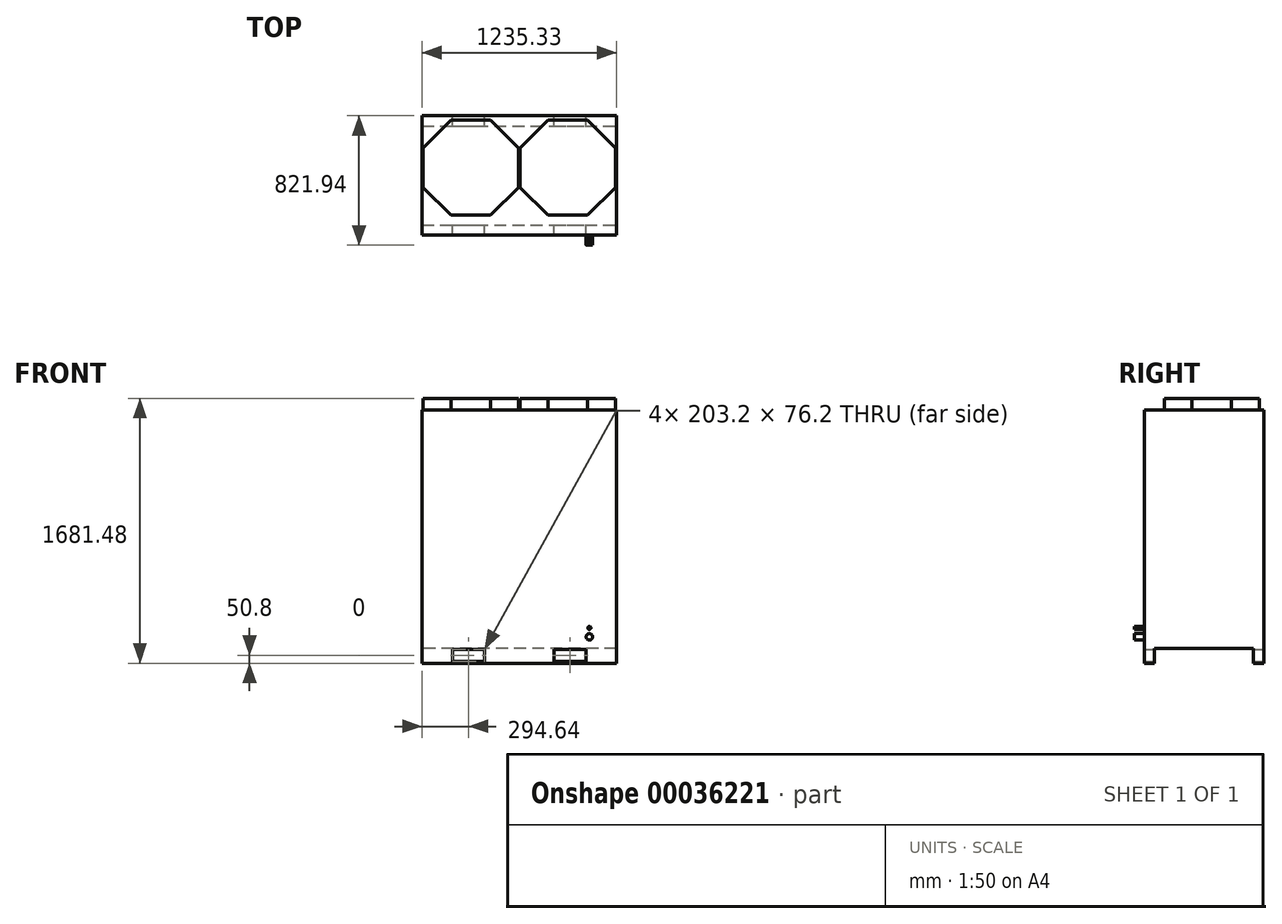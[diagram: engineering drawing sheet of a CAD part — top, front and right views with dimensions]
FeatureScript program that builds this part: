
annotation { "Feature Type Name" : "Feature", "Feature Type Description" : "" }
export const myFeature = defineFeature(function(context is Context, id is Id, definition is map)
    precondition{}
    {
        {
            var Q0;
            Q0=qCreatedBy(makeId("Front.planeOp"),FACE);
            var sketch = newSketch(context, id + "F0", { "sketchPlane" : qUnion([Q0])});
            skLineSegment(sketch, "E0.bottom", {"start": v(0, 0) * mm, "end": v(1235.33, 0) * mm});
            skLineSegment(sketch, "E0.top", {"start": v(0, 1610.36) * mm, "end": v(1235.33, 1610.36) * mm});
            skLineSegment(sketch, "E0.left", {"start": v(0, 0) * mm, "end": v(0, 1610.36) * mm});
            skLineSegment(sketch, "E0.right", {"start": v(1235.33, 0) * mm, "end": v(1235.33, 1610.36) * mm});
            skLineSegment(sketch, "E1.bottom", {"start": v(193.04, 88.9) * mm, "end": v(396.24, 88.9) * mm});
            skLineSegment(sketch, "E1.top", {"start": v(193.04, 12.7) * mm, "end": v(396.24, 12.7) * mm});
            skLineSegment(sketch, "E1.left", {"start": v(193.04, 88.9) * mm, "end": v(193.04, 12.7) * mm});
            skLineSegment(sketch, "E1.right", {"start": v(396.24, 88.9) * mm, "end": v(396.24, 12.7) * mm});
            skLineSegment(sketch, "E2.bottom", {"start": v(839.09, 88.9) * mm, "end": v(1042.29, 88.9) * mm});
            skLineSegment(sketch, "E2.top", {"start": v(839.09, 12.7) * mm, "end": v(1042.29, 12.7) * mm});
            skLineSegment(sketch, "E2.left", {"start": v(839.09, 88.9) * mm, "end": v(839.09, 12.7) * mm});
            skLineSegment(sketch, "E2.right", {"start": v(1042.29, 88.9) * mm, "end": v(1042.29, 12.7) * mm});
            skSolve(sketch);
        }
        {
            var Q0;
            Q0 = qSketchRegion(id + "F0", true);
            extrude(context, id + "F1", {"entities" : qUnion([Q0]), "depth" : 758.44 * mm});
        }
        {
            var Q0;
            Q0=makeQuery(id+"F1.opExtrude","SWEPT_FACE",FACE,{"disambiguationData":[OSD([sQuery(id+"F0.wireOp",EDGE,"E0.left")])]});
            var sketch = newSketch(context, id + "F2", { "sketchPlane" : qUnion([Q0])});
            skLineSegment(sketch, "E3.bottom", {"start": v(64.77, -107.44) * mm, "end": v(693.67, -107.44) * mm});
            skLineSegment(sketch, "E3.top", {"start": v(64.77, 95.76) * mm, "end": v(693.67, 95.76) * mm});
            skLineSegment(sketch, "E3.left", {"start": v(64.77, -107.44) * mm, "end": v(64.77, 95.76) * mm});
            skLineSegment(sketch, "E3.right", {"start": v(693.67, -107.44) * mm, "end": v(693.67, 95.76) * mm});
            skSolve(sketch);
        }
        {
            var Q0;
            Q0 = qSketchRegion(id + "F2", true);
            extrude(context, id + "F3", {"entities" : qUnion([Q0]), "operationType" : NewBodyOperationType.REMOVE, "endBound" : BoundingType.THROUGH_ALL, "oppositeDirection" : true, "depth" : 25.4 * mm});
        }
        {
            var Q0;
            Q0=makeQuery(id+"F1.opExtrude","SWEPT_FACE",FACE,{"disambiguationData":[OSD([sQuery(id+"F0.wireOp",EDGE,"E0.top")])]});
            var sketch = newSketch(context, id + "F4", { "sketchPlane" : qUnion([Q0])});
            skCircle(sketch, "E4.cCircle", {"center": v(309.88, -330.2) * mm, "radius": 302.26 * mm, "construction": true});
            skLineSegment(sketch, "E4.0", {"start": v(612.14, -455.4) * mm, "end": v(435.08, -632.46) * mm});
            skLineSegment(sketch, "E4.1", {"start": v(435.08, -632.46) * mm, "end": v(184.68, -632.46) * mm});
            skLineSegment(sketch, "E4.2", {"start": v(184.68, -632.46) * mm, "end": v(7.62, -455.4) * mm});
            skLineSegment(sketch, "E4.3", {"start": v(7.62, -455.4) * mm, "end": v(7.62, -205) * mm});
            skLineSegment(sketch, "E4.4", {"start": v(7.62, -205) * mm, "end": v(184.68, -27.94) * mm});
            skLineSegment(sketch, "E4.5", {"start": v(184.68, -27.94) * mm, "end": v(435.08, -27.94) * mm});
            skLineSegment(sketch, "E4.6", {"start": v(435.08, -27.94) * mm, "end": v(612.14, -205) * mm});
            skLineSegment(sketch, "E4.7", {"start": v(612.14, -205) * mm, "end": v(612.14, -455.4) * mm});
            skPoint(sketch, "E4.0.midPoint", {"position": v(523.61, -543.93) * mm});
            skCircle(sketch, "E5.cCircle", {"center": v(925.45, -330.2) * mm, "radius": 302.26 * mm, "construction": true});
            skLineSegment(sketch, "E5.0", {"start": v(1227.7, -455.4) * mm, "end": v(1050.65, -632.46) * mm});
            skLineSegment(sketch, "E5.1", {"start": v(1050.65, -632.46) * mm, "end": v(800.25, -632.46) * mm});
            skLineSegment(sketch, "E5.2", {"start": v(800.25, -632.46) * mm, "end": v(623.19, -455.4) * mm});
            skLineSegment(sketch, "E5.3", {"start": v(623.19, -455.4) * mm, "end": v(623.19, -205) * mm});
            skLineSegment(sketch, "E5.4", {"start": v(623.19, -205) * mm, "end": v(800.25, -27.94) * mm});
            skLineSegment(sketch, "E5.5", {"start": v(800.25, -27.94) * mm, "end": v(1050.65, -27.94) * mm});
            skLineSegment(sketch, "E5.6", {"start": v(1050.65, -27.94) * mm, "end": v(1227.7, -205) * mm});
            skLineSegment(sketch, "E5.7", {"start": v(1227.7, -205) * mm, "end": v(1227.7, -455.4) * mm});
            skPoint(sketch, "E5.0.midPoint", {"position": v(1139.18, -543.93) * mm});
            skSolve(sketch);
        }
        {
            var Q0;
            Q0 = qSketchRegion(id + "F4", true);
            extrude(context, id + "F5", {"entities" : qUnion([Q0]), "operationType" : NewBodyOperationType.ADD, "depth" : 71.12 * mm});
        }
        {
            var Q0;
            Q0=makeQuery(id+"F1.opExtrude","CAP_FACE",FACE,{"disambiguationData":[OSD([sQuery(id+"F0.wireOp",EDGE,"E0.bottom"),sQuery(id+"F0.wireOp",EDGE,"E0.top"),sQuery(id+"F0.wireOp",EDGE,"E0.left"),sQuery(id+"F0.wireOp",EDGE,"E0.right"),sQuery(id+"F0.wireOp",EDGE,"E1.bottom"),sQuery(id+"F0.wireOp",EDGE,"E1.top"),sQuery(id+"F0.wireOp",EDGE,"E1.left"),sQuery(id+"F0.wireOp",EDGE,"E1.right"),sQuery(id+"F0.wireOp",EDGE,"E2.bottom"),sQuery(id+"F0.wireOp",EDGE,"E2.top"),sQuery(id+"F0.wireOp",EDGE,"E2.left"),sQuery(id+"F0.wireOp",EDGE,"E2.right")])],"isStart":false});
            var sketch = newSketch(context, id + "F6", { "sketchPlane" : qUnion([Q0])});
            skCircle(sketch, "E6", {"center": v(1063, 167.64) * mm, "radius": 20.64 * mm});
            skCircle(sketch, "E7", {"center": v(1063, 224.8) * mm, "radius": 9.53 * mm});
            skSolve(sketch);
        }
        {
            var Q0;
            Q0 = qSketchRegion(id + "F6", true);
            extrude(context, id + "F7", {"entities" : qUnion([Q0]), "operationType" : NewBodyOperationType.ADD, "depth" : 63.5 * mm});
        }
    });
